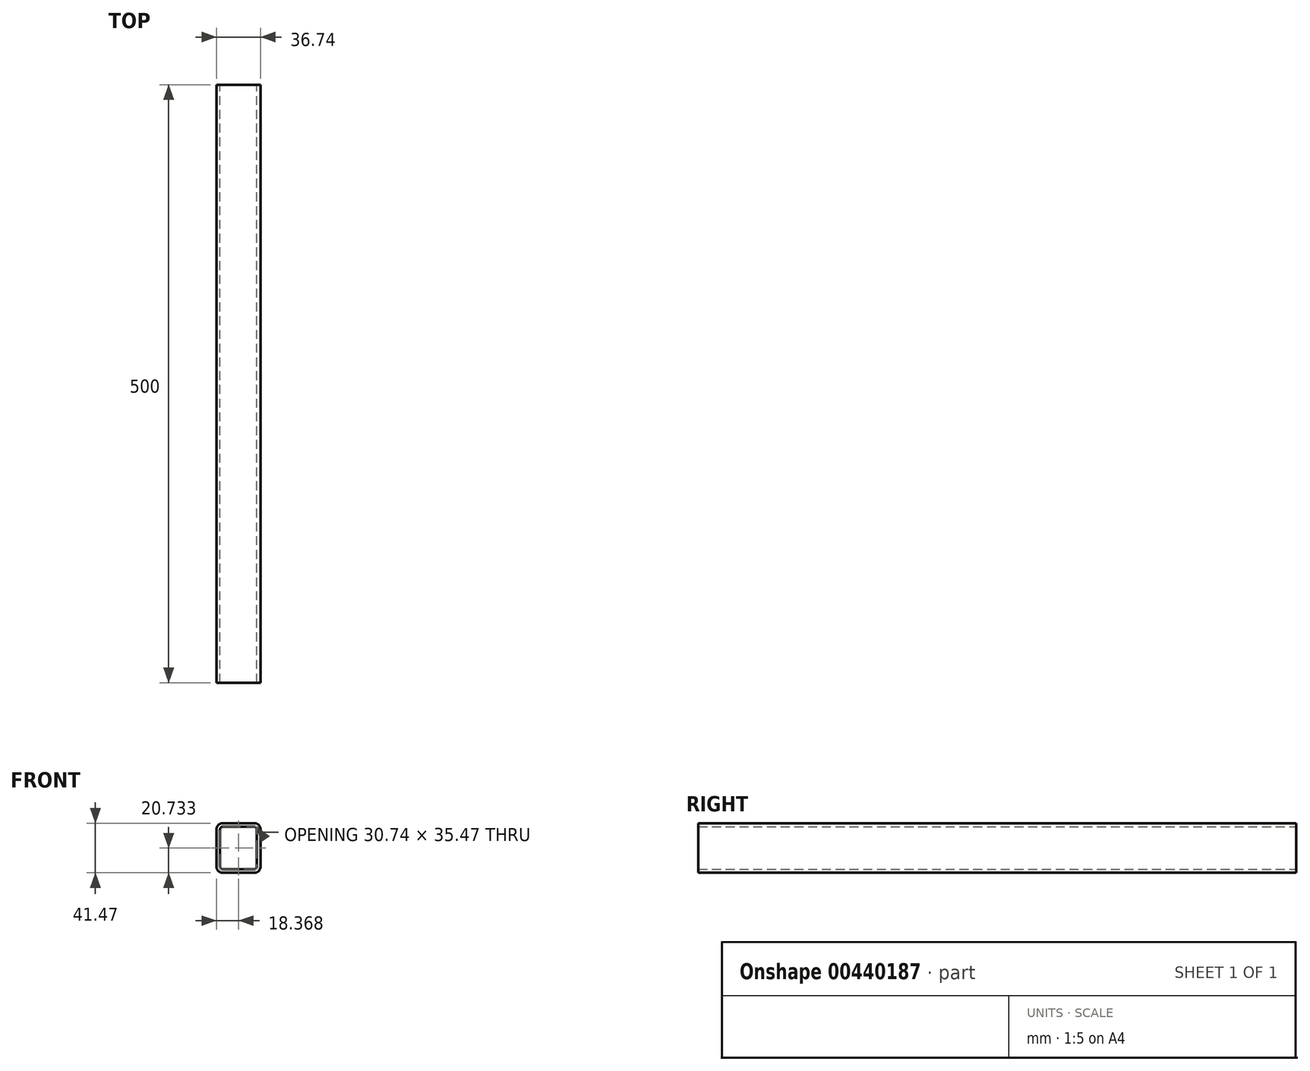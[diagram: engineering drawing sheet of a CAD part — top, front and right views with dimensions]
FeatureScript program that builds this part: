
annotation { "Feature Type Name" : "Feature", "Feature Type Description" : "" }
export const myFeature = defineFeature(function(context is Context, id is Id, definition is map)
    precondition{}
    {
        {
            var Q0;
            Q0=qCreatedBy(makeId("Front.planeOp"),FACE);
            var sketch = newSketch(context, id + "F0", { "sketchPlane" : qUnion([Q0])});
            skLineSegment(sketch, "E0.bottom", {"start": v(36.74, 41.47) * mm, "end": v(0, 41.47) * mm});
            skLineSegment(sketch, "E0.top", {"start": v(36.74, 0) * mm, "end": v(0, 0) * mm});
            skLineSegment(sketch, "E0.left", {"start": v(36.74, 41.47) * mm, "end": v(36.74, 0) * mm});
            skLineSegment(sketch, "E0.right", {"start": v(0, 41.47) * mm, "end": v(0, 0) * mm});
            skSolve(sketch);
        }
        {
            var Q0;
            Q0=makeQuery(id+"F0.imprint","IMPRINT",FACE,{"disambiguationData":[TD([[makeQuery(id+"F0.imprint","IMPRINT",EDGE,{"derivedFrom":sQuery(id+"F0.wireOp",EDGE,"E0.bottom")}),1.0]])]});
            extrude(context, id + "F1", {"entities" : qUnion([Q0]), "depth" : 500 * mm});
        }
        {
            var Q0;
            Q0=makeQuery(id+"F1.opExtrude","SWEPT_EDGE",EDGE,{"disambiguationData":[OSD([sQuery(id+"F0.wireOp",EDGE,"E0.bottom"),sQuery(id+"F0.wireOp",EDGE,"E0.left")])]});
            var Q1;
            Q1=makeQuery(id+"F1.opExtrude","SWEPT_EDGE",EDGE,{"disambiguationData":[OSD([sQuery(id+"F0.wireOp",EDGE,"E0.bottom"),sQuery(id+"F0.wireOp",EDGE,"E0.right")])]});
            var Q2;
            Q2=makeQuery(id+"F1.opExtrude","SWEPT_EDGE",EDGE,{"disambiguationData":[OSD([sQuery(id+"F0.wireOp",EDGE,"E0.top"),sQuery(id+"F0.wireOp",EDGE,"E0.left")])]});
            var Q3;
            Q3=makeQuery(id+"F1.opExtrude","SWEPT_EDGE",EDGE,{"disambiguationData":[OSD([sQuery(id+"F0.wireOp",EDGE,"E0.top"),sQuery(id+"F0.wireOp",EDGE,"E0.right")])]});
            fillet(context, id + "F2", {"entities" : qUnion([Q0, Q1, Q2, Q3]), "radius" : 5 * mm, "tangentPropagation" : true, "allowEdgeOverflow" : false});
        }
        {
            var Q0;
            Q0=makeQuery(id+"F1.opExtrude","CAP_FACE",FACE,{"disambiguationData":[OSD([sQuery(id+"F0.wireOp",EDGE,"E0.bottom"),sQuery(id+"F0.wireOp",EDGE,"E0.top"),sQuery(id+"F0.wireOp",EDGE,"E0.left"),sQuery(id+"F0.wireOp",EDGE,"E0.right")])],"isStart":false});
            var Q1;
            Q1=makeQuery(id+"F1.opExtrude","CAP_FACE",FACE,{"disambiguationData":[OSD([sQuery(id+"F0.wireOp",EDGE,"E0.bottom"),sQuery(id+"F0.wireOp",EDGE,"E0.top"),sQuery(id+"F0.wireOp",EDGE,"E0.left"),sQuery(id+"F0.wireOp",EDGE,"E0.right")])],"isStart":true});
            shell(context, id + "F3", {"entities" : qUnion([Q0, Q1]), "thickness" : 3 * mm});
        }
    });
